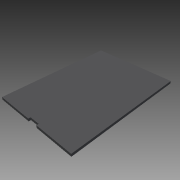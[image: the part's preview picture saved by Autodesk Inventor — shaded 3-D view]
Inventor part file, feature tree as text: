
AUTODESK INVENTOR PART (.ipt)
format: ipt  version: 2013 (Build 170138000, 138)  size: 92,672 bytes
history: native  units: mm
features: extrude x3, sketch x3, reference x2
ambient origin geometry x8: Origin, YZ Plane, XZ Plane, XY Plane, X Axis, Y Axis, Z Axis, Center Point
bodies: Solid1 (feature_tree)
feature tree (8):
  extrude  "Extrusion1"  Depth=552.45mm
  extrude  "Extrusion2"  Depth=9.525mm TaperAngle=0.0deg
  extrude  "Extrusion3"  [1 undecoded]
  sketch  "Sketch1"  dims[d0=395.544mm d2=552.45mm]
  sketch  "Sketch2"  dims[d3=12.5mm d4=0.0mm d5=9.525mm d6=0.0mm]
  reference  "Reference1"
  sketch  "Sketch3"  dims[d7=7.0mm d8=0.0mm]
  reference  "Reference2"
note: 1 required parameter value undecoded (feature->parameter linkage not recoverable at this tier; creation-order binding heuristic only, values carry confidence <= 0.55)
